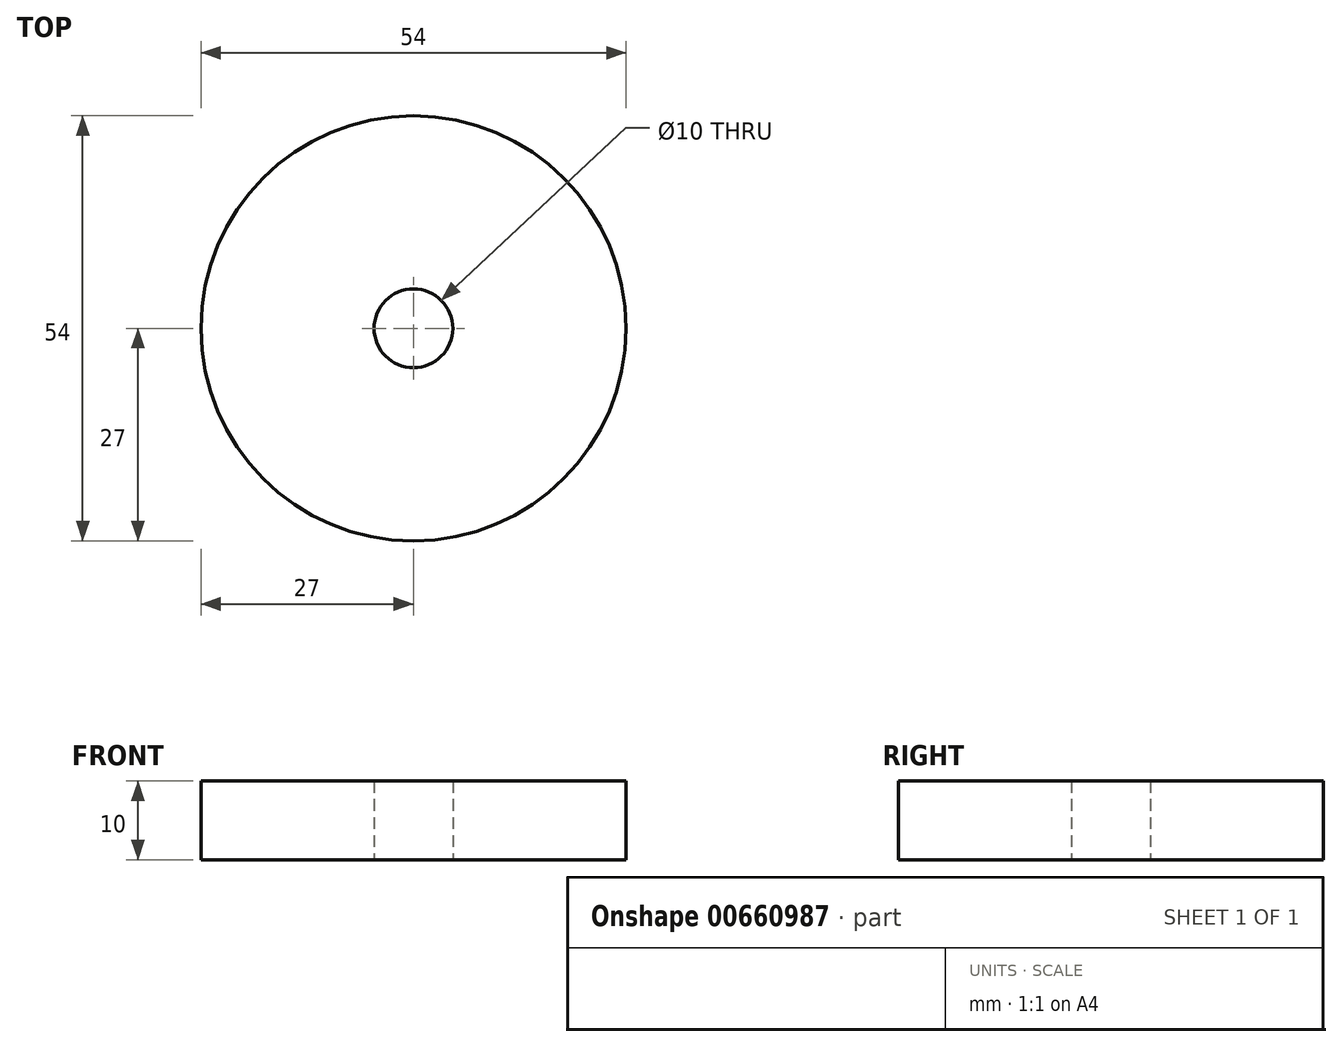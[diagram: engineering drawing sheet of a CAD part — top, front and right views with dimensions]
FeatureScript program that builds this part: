
annotation { "Feature Type Name" : "Feature", "Feature Type Description" : "" }
export const myFeature = defineFeature(function(context is Context, id is Id, definition is map)
    precondition{}
    {
        {
            var Q0;
            Q0=qCreatedBy(makeId("Top.planeOp"),FACE);
            var sketch = newSketch(context, id + "F0", { "sketchPlane" : qUnion([Q0])});
            skCircle(sketch, "E0", {"center": v(0, 0) * mm, "radius": 5 * mm});
            skCircle(sketch, "E1", {"center": v(0, 0) * mm, "radius": 27 * mm});
            skSolve(sketch);
        }
        {
            var Q0;
            Q0=makeQuery(id+"F0.imprint","IMPRINT",FACE,{"disambiguationData":[TD([[makeQuery(id+"F0.imprint","IMPRINT",EDGE,{"derivedFrom":sQuery(id+"F0.wireOp",EDGE,"E0")}),-1.0]])]});
            extrude(context, id + "F1", {"entities" : qUnion([Q0]), "depth" : 10 * mm, "offsetDistance" : 25 * mm});
        }
    });
